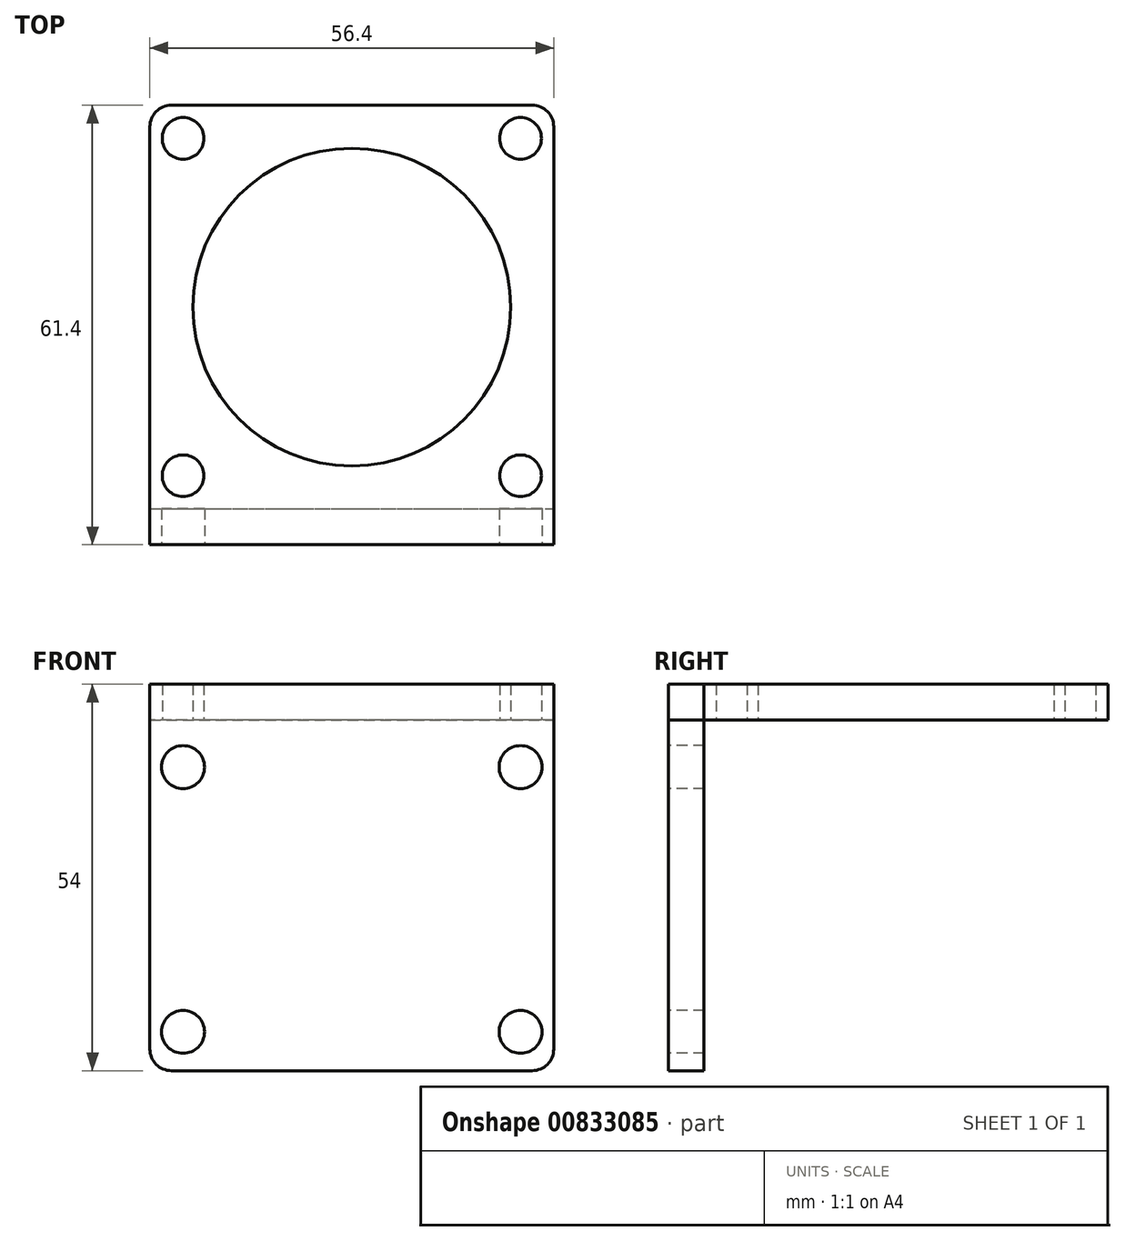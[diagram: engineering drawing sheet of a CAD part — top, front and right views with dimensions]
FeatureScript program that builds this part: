
annotation { "Feature Type Name" : "Feature", "Feature Type Description" : "" }
export const myFeature = defineFeature(function(context is Context, id is Id, definition is map)
    precondition{}
    {
        {
            var Q0;
            Q0=qCreatedBy(makeId("Top.planeOp"),FACE);
            var sketch = newSketch(context, id + "F0", { "sketchPlane" : qUnion([Q0])});
            skLineSegment(sketch, "E0.bottom", {"start": v(28.2, -28.2) * mm, "end": v(-28.2, -28.2) * mm});
            skLineSegment(sketch, "E0.top", {"start": v(28.2, 28.2) * mm, "end": v(-28.2, 28.2) * mm});
            skLineSegment(sketch, "E0.left", {"start": v(28.2, -28.2) * mm, "end": v(28.2, 28.2) * mm});
            skLineSegment(sketch, "E0.right", {"start": v(-28.2, -28.2) * mm, "end": v(-28.2, 28.2) * mm});
            skPoint(sketch, "E0.middle", {"position": v(0, 0) * mm});
            skCircle(sketch, "E1", {"center": v(-23.57, 23.57) * mm, "radius": 2.91 * mm});
            skCircle(sketch, "E2", {"center": v(23.57, 23.57) * mm, "radius": 2.91 * mm});
            skCircle(sketch, "E3", {"center": v(-23.57, -23.57) * mm, "radius": 2.91 * mm});
            skCircle(sketch, "E4", {"center": v(23.57, -23.57) * mm, "radius": 2.91 * mm});
            skCircle(sketch, "E5", {"center": v(0, 0) * mm, "radius": 22.2 * mm});
            skLineSegment(sketch, "E6.bottom", {"start": v(-28.2, -28.2) * mm, "end": v(28.2, -28.2) * mm});
            skLineSegment(sketch, "E6.top", {"start": v(-28.2, -33.2) * mm, "end": v(28.2, -33.2) * mm});
            skLineSegment(sketch, "E6.left", {"start": v(-28.2, -28.2) * mm, "end": v(-28.2, -33.2) * mm});
            skLineSegment(sketch, "E6.right", {"start": v(28.2, -28.2) * mm, "end": v(28.2, -33.2) * mm});
            skSolve(sketch);
        }
        {
            var Q0;
            Q0=makeQuery(id+"F0.imprint","IMPRINT",FACE,{"disambiguationData":[TD([[makeQuery(id+"F0.imprint","IMPRINT",EDGE,{"derivedFrom":sQuery(id+"F0.wireOp",EDGE,"E0.top")}),1.0]])]});
            var Q1;
            Q1=makeQuery(id+"F0.imprint","IMPRINT",FACE,{"disambiguationData":[TD([[makeQuery(id+"F0.imprint","IMPRINT",EDGE,{"derivedFrom":sQuery(id+"F0.wireOp",EDGE,"E6.top")}),1.0]])]});
            extrude(context, id + "F1", {"entities" : qUnion([Q0, Q1]), "depth" : 5 * mm, "offsetDistance" : 25 * mm});
        }
        {
            var Q0;
            Q0=makeQuery(id+"F1.opExtrude","SWEPT_FACE",FACE,{"disambiguationData":[OSD([sQuery(id+"F0.wireOp",EDGE,"E6.top")])]});
            var sketch = newSketch(context, id + "F2", { "sketchPlane" : qUnion([Q0])});
            skLineSegment(sketch, "E7.bottom", {"start": v(-28.2, 5) * mm, "end": v(28.2, 5) * mm});
            skLineSegment(sketch, "E7.top", {"start": v(-28.2, -49) * mm, "end": v(28.2, -49) * mm});
            skLineSegment(sketch, "E7.left", {"start": v(-28.2, 5) * mm, "end": v(-28.2, -49) * mm});
            skLineSegment(sketch, "E7.right", {"start": v(28.2, 5) * mm, "end": v(28.2, -49) * mm});
            skPoint(sketch, "E8.middle", {"position": v(0, -25.08) * mm});
            skCircle(sketch, "E9", {"center": v(-23.57, -6.58) * mm, "radius": 3 * mm});
            skCircle(sketch, "E10", {"center": v(-23.57, -43.58) * mm, "radius": 3 * mm});
            skCircle(sketch, "E11", {"center": v(23.57, -43.58) * mm, "radius": 3 * mm});
            skCircle(sketch, "E12", {"center": v(23.57, -6.58) * mm, "radius": 3 * mm});
            skSolve(sketch);
        }
        {
            var Q0;
            {var subQ1=sQuery(id+"F2.wireOp",EDGE,"E7.top");Q0=makeQuery(id+"F2.imprint","IMPRINT",FACE,{"disambiguationData":[TD([[makeQuery(id+"F2.imprint","IMPRINT",EDGE,{"derivedFrom":subQ1}),1.0]])]});}
            extrude(context, id + "F3", {"entities" : qUnion([Q0]), "operationType" : NewBodyOperationType.ADD, "oppositeDirection" : true, "depth" : 5 * mm, "offsetDistance" : 25 * mm});
        }
        {
            var Q0;
            Q0=makeQuery(id+"F1.opExtrude","SWEPT_EDGE",EDGE,{"disambiguationData":[OSD([sQuery(id+"F0.wireOp",EDGE,"E0.top"),sQuery(id+"F0.wireOp",EDGE,"E0.right")])]});
            var Q1;
            Q1=makeQuery(id+"F1.opExtrude","SWEPT_EDGE",EDGE,{"disambiguationData":[OSD([sQuery(id+"F0.wireOp",EDGE,"E0.top"),sQuery(id+"F0.wireOp",EDGE,"E0.left")])]});
            var Q2;
            Q2=makeQuery(id+"F3.opExtrude","SWEPT_EDGE",EDGE,{"disambiguationData":[OSD([sQuery(id+"F2.wireOp",EDGE,"E7.top"),sQuery(id+"F2.wireOp",EDGE,"E7.left")])]});
            var Q3;
            Q3=makeQuery(id+"F3.opExtrude","SWEPT_EDGE",EDGE,{"disambiguationData":[OSD([sQuery(id+"F2.wireOp",EDGE,"E7.top"),sQuery(id+"F2.wireOp",EDGE,"E7.right")])]});
            fillet(context, id + "F4", {"entities" : qUnion([Q0, Q1, Q2, Q3]), "radius" : 3 * mm, "tangentPropagation" : true, "allowEdgeOverflow" : false});
        }
    });
